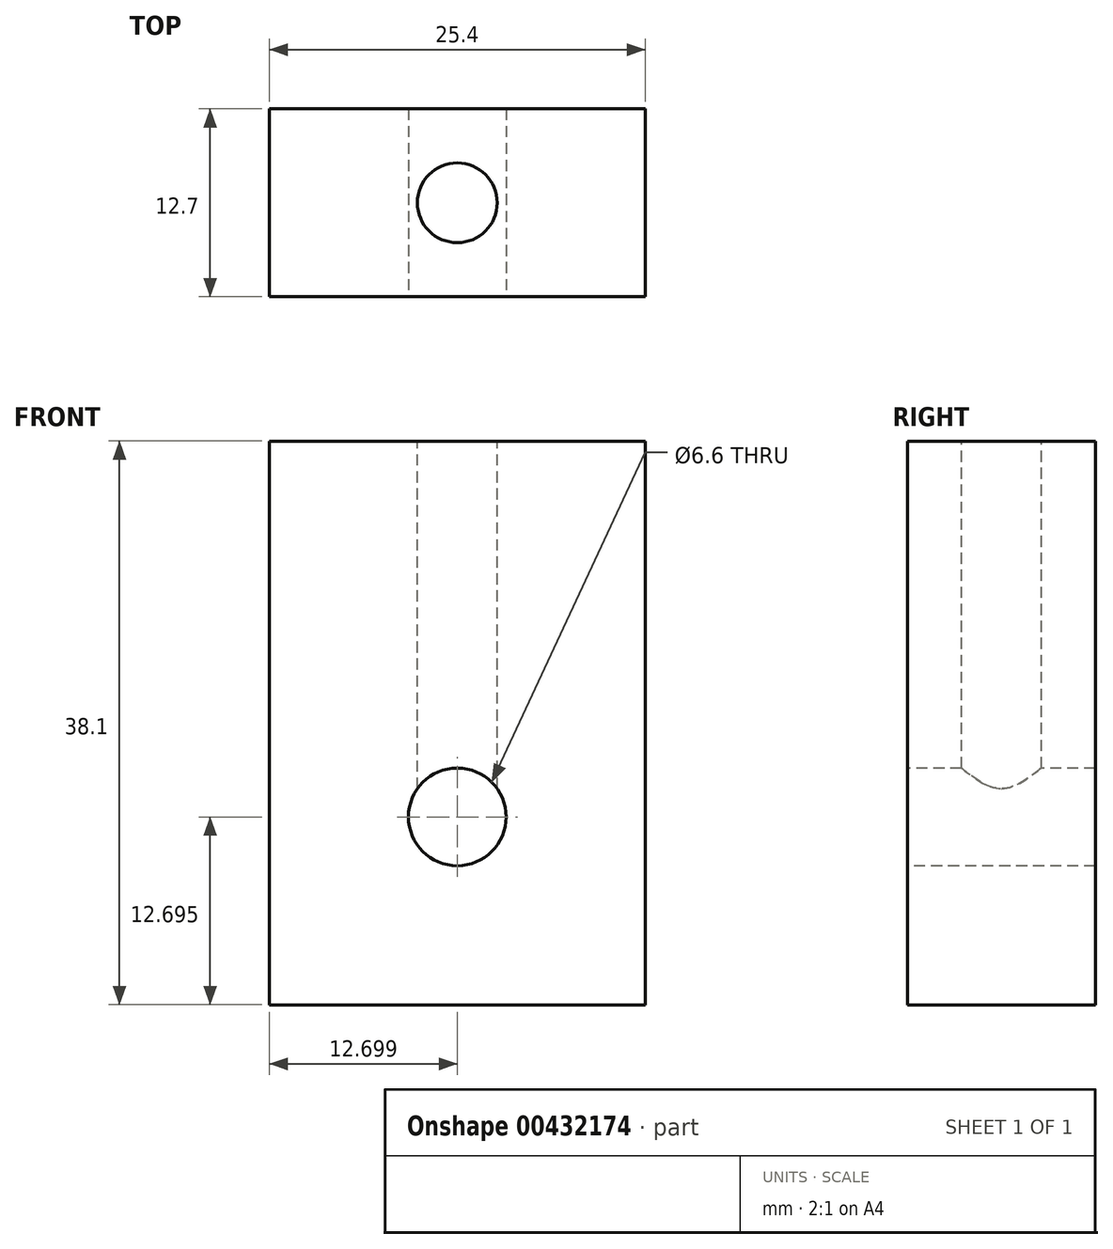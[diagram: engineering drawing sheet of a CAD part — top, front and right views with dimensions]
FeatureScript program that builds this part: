
annotation { "Feature Type Name" : "Feature", "Feature Type Description" : "" }
export const myFeature = defineFeature(function(context is Context, id is Id, definition is map)
    precondition{}
    {
        {
            var Q0;
            Q0=qCreatedBy(makeId("Front.planeOp"),FACE);
            var sketch = newSketch(context, id + "F0", { "sketchPlane" : qUnion([Q0])});
            skLineSegment(sketch, "E0.bottom", {"start": v(-9.6, 19.92) * mm, "end": v(15.8, 19.92) * mm});
            skLineSegment(sketch, "E0.top", {"start": v(-9.6, -18.18) * mm, "end": v(15.8, -18.18) * mm});
            skLineSegment(sketch, "E0.left", {"start": v(-9.6, 19.92) * mm, "end": v(-9.6, -18.18) * mm});
            skLineSegment(sketch, "E0.right", {"start": v(15.8, 19.92) * mm, "end": v(15.8, -18.18) * mm});
            skSolve(sketch);
        }
        {
            var Q0;
            Q0=makeQuery(id+"F0.imprint","IMPRINT",FACE,{"disambiguationData":[TD([[makeQuery(id+"F0.imprint","IMPRINT",EDGE,{"derivedFrom":sQuery(id+"F0.wireOp",EDGE,"E0.bottom")}),-1.0]])]});
            extrude(context, id + "F1", {"entities" : qUnion([Q0]), "depth" : 12.7 * mm});
        }
        {
            var Q0;
            Q0=makeQuery(id+"F1.opExtrude","CAP_FACE",FACE,{"disambiguationData":[OSD([sQuery(id+"F0.wireOp",EDGE,"E0.bottom"),sQuery(id+"F0.wireOp",EDGE,"E0.top"),sQuery(id+"F0.wireOp",EDGE,"E0.left"),sQuery(id+"F0.wireOp",EDGE,"E0.right")])],"isStart":false});
            var sketch = newSketch(context, id + "F2", { "sketchPlane" : qUnion([Q0])});
            skCircle(sketch, "E1", {"center": v(3.1, -5.48) * mm, "radius": 3.3 * mm});
            skSolve(sketch);
        }
        {
            var Q0;
            Q0=makeQuery(id+"F2.imprint","IMPRINT",FACE,{"disambiguationData":[TD([[makeQuery(id+"F2.imprint","IMPRINT",EDGE,{"derivedFrom":sQuery(id+"F2.wireOp",EDGE,"E1")}),1.0]])]});
            var Q1;
            Q1=sQuery(id+"F2.wireOp",EDGE,"E1");
            extrude(context, id + "F3", {"entities" : qUnion([Q0]), "operationType" : NewBodyOperationType.REMOVE, "surfaceEntities" : qUnion([Q1]), "oppositeDirection" : true, "depth" : 25.4 * mm});
        }
        {
            var Q0;
            Q0=makeQuery(id+"F1.opExtrude","SWEPT_FACE",FACE,{"disambiguationData":[OSD([sQuery(id+"F0.wireOp",EDGE,"E0.bottom")])]});
            var sketch = newSketch(context, id + "F4", { "sketchPlane" : qUnion([Q0])});
            skCircle(sketch, "E2", {"center": v(3.1, -6.35) * mm, "radius": 2.7 * mm});
            skSolve(sketch);
        }
        {
            var Q0;
            Q0=makeQuery(id+"F4.imprint","IMPRINT",FACE,{"disambiguationData":[TD([[makeQuery(id+"F4.imprint","IMPRINT",EDGE,{"derivedFrom":sQuery(id+"F4.wireOp",EDGE,"E2")}),1.0]])]});
            var Q1;
            Q1=sQuery(id+"F4.wireOp",EDGE,"E2");
            extrude(context, id + "F5", {"entities" : qUnion([Q0]), "operationType" : NewBodyOperationType.REMOVE, "surfaceEntities" : qUnion([Q1]), "oppositeDirection" : true, "depth" : 25.4 * mm});
        }
    });
